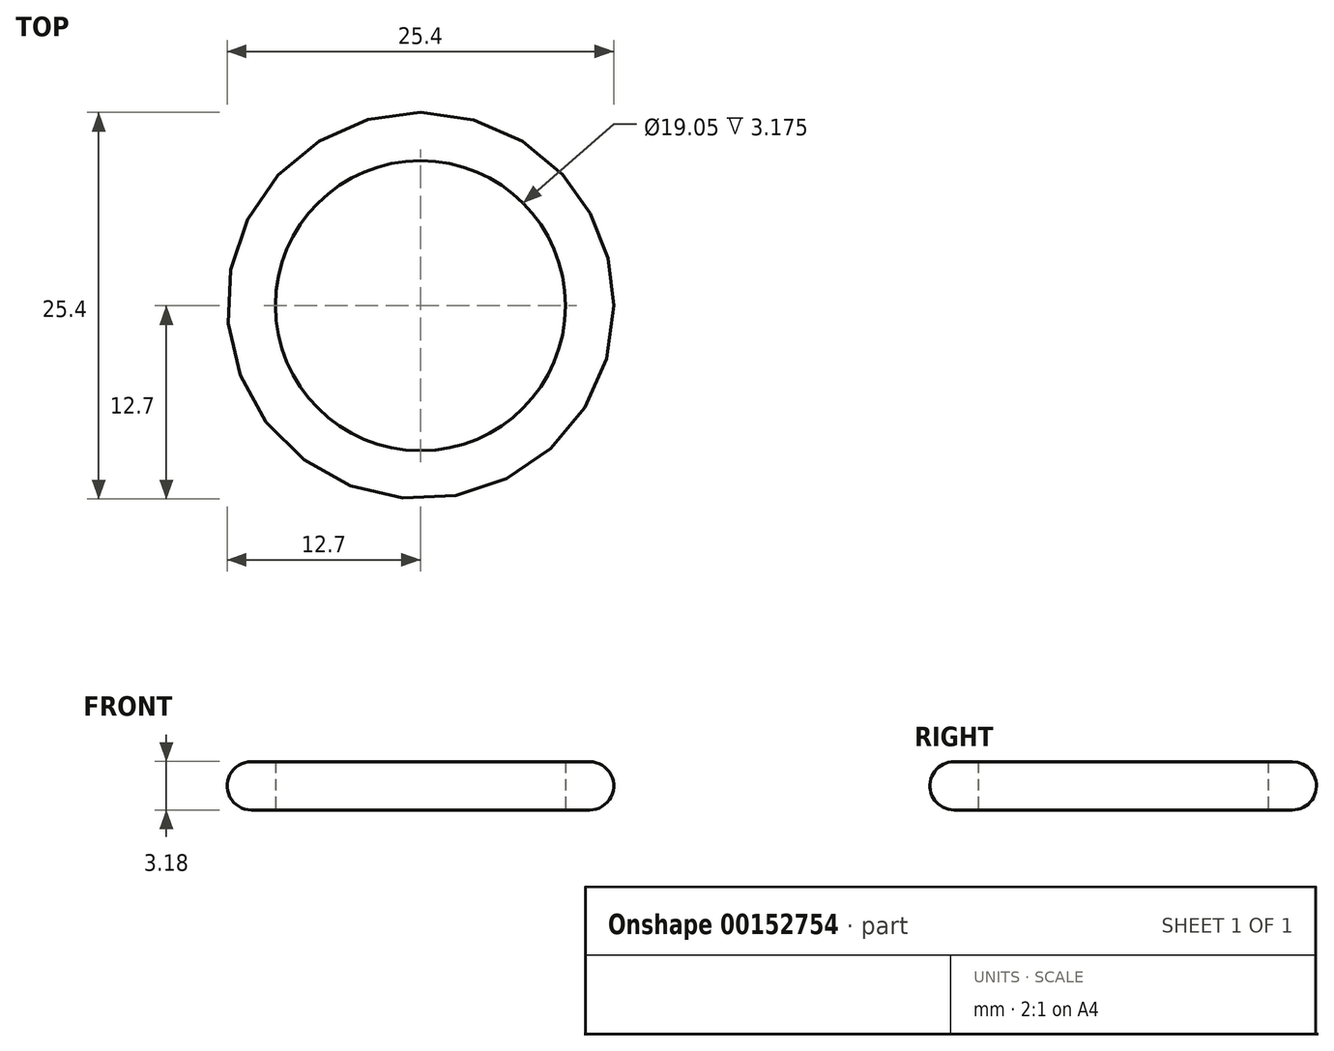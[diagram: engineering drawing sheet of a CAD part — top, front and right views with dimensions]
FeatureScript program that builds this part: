
annotation { "Feature Type Name" : "Feature", "Feature Type Description" : "" }
export const myFeature = defineFeature(function(context is Context, id is Id, definition is map)
    precondition{}
    {
        {
            var Q0;
            Q0=qCreatedBy(makeId("Top.planeOp"),FACE);
            var sketch = newSketch(context, id + "F0", { "sketchPlane" : qUnion([Q0])});
            skCircle(sketch, "E0", {"center": v(0, 0) * mm, "radius": 9.53 * mm});
            skCircle(sketch, "E1", {"center": v(0, 0) * mm, "radius": 12.7 * mm});
            skSolve(sketch);
        }
        {
            var Q0;
            Q0=qSketchRegion(id+"F0",true);
            extrude(context, id + "F1", {"entities" : qUnion([Q0]), "depth" : 3.17 * mm});
        }
        {
            var Q0;
            Q0=makeQuery(id+"F1.opExtrude","CAP_EDGE",EDGE,{"disambiguationData":[OSD([sQuery(id+"F0.wireOp",EDGE,"E1")])],"isStart":true});
            var Q1;
            Q1=makeQuery(id+"F1.opExtrude","CAP_EDGE",EDGE,{"disambiguationData":[OSD([sQuery(id+"F0.wireOp",EDGE,"E1")])],"isStart":false});
            fillet(context, id + "F2", {"entities" : qUnion([Q0, Q1]), "radius" : 1.59 * mm, "tangentPropagation" : true, "allowEdgeOverflow" : false});
        }
    });
